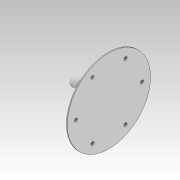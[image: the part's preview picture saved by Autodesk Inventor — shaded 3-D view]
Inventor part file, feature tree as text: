
AUTODESK INVENTOR PART (.ipt)
format: ipt  version: 2020 (Build 240168000, 168)  size: 158,720 bytes
history: native  units: mm
features: sketch x3, extrude x2, revolve x1, plane x1, pattern_circular x1
ambient origin geometry x8: Origin, YZ Plane, XZ Plane, XY Plane, X Axis, Y Axis, Z Axis, Center Point
bodies: Solid1 (feature_tree)
feature tree (8):
  revolve  "Revolution1"  [1 undecoded]
  extrude  "Extrusion1"  Depth=3.0mm
  plane  "Work Plane1"
  extrude  "Extrusion2"  Depth=10.0mm
  pattern_circular  "Circular Pattern1"  Angle=90.0deg  [1 undecoded]
  sketch  "Sketch1"  dims[d0=44.0mm d1=5.0mm]
  sketch  "Sketch2"  dims[d2=3.0mm d3=1.0mm]
  sketch  "Sketch3"  dims[d4=35.0mm d5=10.0mm d6=90.0deg d7=3.3mm d8=35.0mm d9=0.0mm d10=0.0mm d11=-2.0mm d12=6.0mm d13=2.0mm d14=0.0mm d15=60.0mm d16=360.0deg d18=5.0mm]
note: 2 required parameter values undecoded (feature->parameter linkage not recoverable at this tier; creation-order binding heuristic only, values carry confidence <= 0.55)